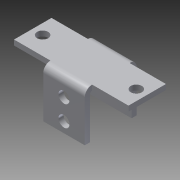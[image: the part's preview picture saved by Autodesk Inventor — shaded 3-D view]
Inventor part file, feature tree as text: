
AUTODESK INVENTOR PART (.ipt)
format: ipt  version: 2013 (Build 170138000, 138)  size: 257,536 bytes
history: native  units: in
note: dims shown in document units (in); Inventor stores cm internally (conversion verified against a paired STEP export)
features: sheet_metal_op x9, other x7, sketch x6, reference x2, extrude x1
ambient origin geometry x8: Origin, YZ Plane, XZ Plane, XY Plane, X Axis, Y Axis, Z Axis, Center Point
bodies: Solid1 (feature_tree)
feature tree (25):
  sheet_metal_op  "Face1"
  sheet_metal_op  "Flange1"
  sketch  "Sketch3"  dims[d3=0.125in]
  sheet_metal_op  "Flange2"
  extrude  "Extrusion1"  Depth=1.0in
  sheet_metal_op  "Face2"
  sketch  "Sketch1"  dims[d0=1.0in d1=1.0in]
  other  "Plate1"
  sketch  "Sketch2"  dims[d2=0.125in]
  other  "Plate2"
  sheet_metal_op  "Bend1"
  sheet_metal_op  "Corner1"
  sketch  "Sketch4"  dims[d4=0.0625in]
  other  "Plate3"
  sheet_metal_op  "Bend2"
  sheet_metal_op  "Corner2"
  sketch  "Sketch5"  dims[d5=0.25in]
  other  "Plate4"
  sheet_metal_op  "Bend3"
  sketch  "Sketch6"  dims[d6=0.125in d7=1.075in d8=90.0deg d9=0.05in d10=0.5in d11=0.125in d12=0.125in d13=0.25in d14=0.25in d15=0.25in d16=0.266in d17=0.266in d18=0.125in d19=0.0625in d20=0.25in d21=0.125in d22=1.175in d23=90.0deg d24=0.05in d25=0.5in d26=0.125in d27=0.125in d28=1.5in d29=0.0in d30=0.875in d31=0.9in d32=0.875in d33=0.05in d34=0.125in d35=0.0625in d36=0.25in d37=0.125in d38=0.125in d39=0.0in]
  reference  "Reference1"
  reference  "Reference2"
  other  "Cut1"
  other  "Definition1"
  other  "Cut2"
